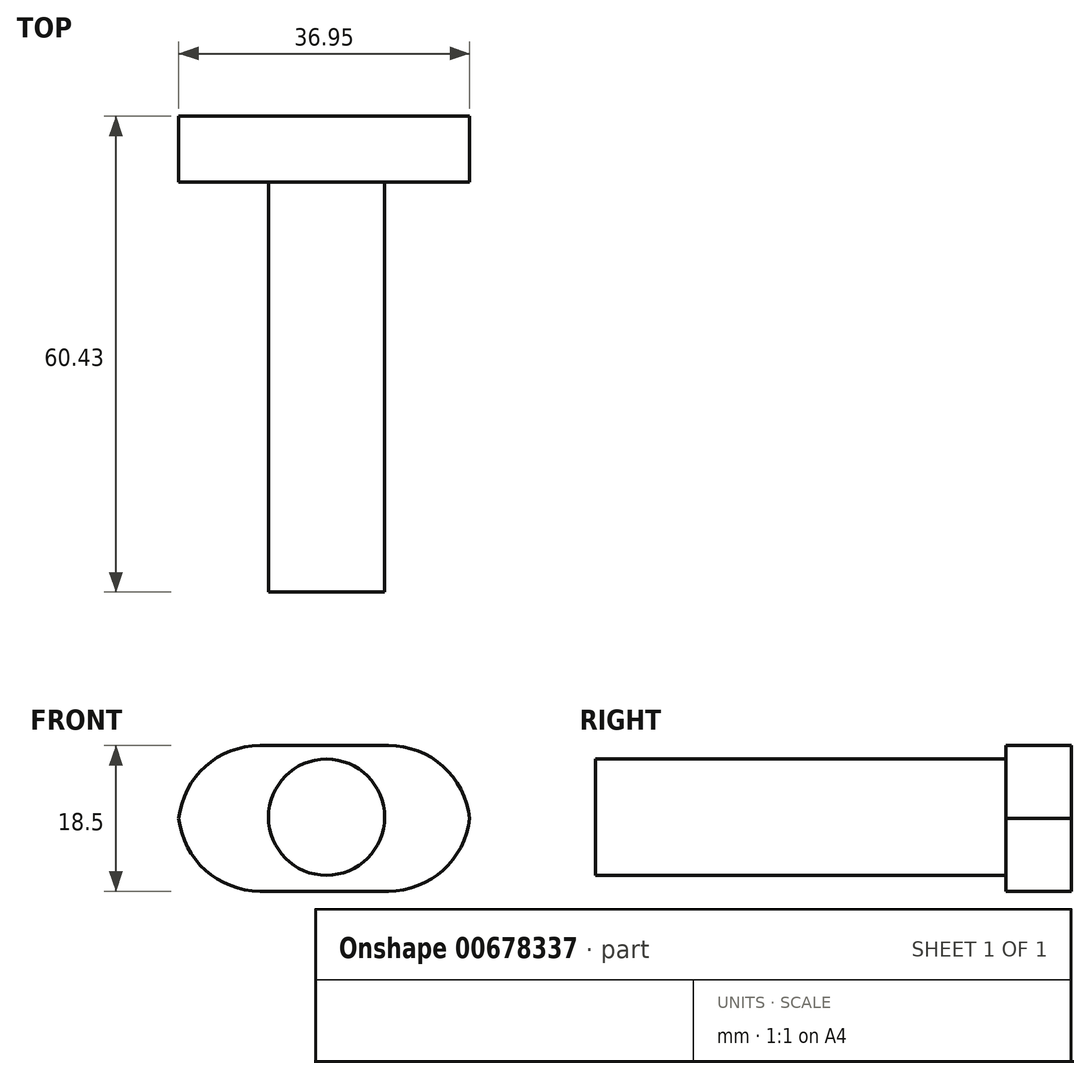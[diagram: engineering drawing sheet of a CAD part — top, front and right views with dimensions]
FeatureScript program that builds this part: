
annotation { "Feature Type Name" : "Feature", "Feature Type Description" : "" }
export const myFeature = defineFeature(function(context is Context, id is Id, definition is map)
    precondition{}
    {
        {
            var Q0;
            Q0=qCreatedBy(makeId("Front.planeOp"),FACE);
            var sketch = newSketch(context, id + "F0", { "sketchPlane" : qUnion([Q0])});
            skCircle(sketch, "E0", {"center": v(0, 0) * mm, "radius": 7.38 * mm});
            skSolve(sketch);
        }
        {
            var Q0;
            Q0=makeQuery(id+"F0.imprint","IMPRINT",FACE,{"disambiguationData":[TD([[makeQuery(id+"F0.imprint","IMPRINT",EDGE,{"derivedFrom":sQuery(id+"F0.wireOp",EDGE,"E0")}),1.0]])]});
            extrude(context, id + "F1", {"entities" : qUnion([Q0]), "depth" : 57.7 * mm, "offsetDistance" : 25 * mm});
        }
        {
            var Q0;
            Q0=qCreatedBy(makeId("Top.planeOp"),FACE);
            var sketch = newSketch(context, id + "F2", { "sketchPlane" : qUnion([Q0])});
            skLineSegment(sketch, "E1.bottom", {"start": v(-18.83, 2.73) * mm, "end": v(18.25, 2.73) * mm});
            skLineSegment(sketch, "E1.top", {"start": v(-18.83, -5.6) * mm, "end": v(18.25, -5.6) * mm});
            skLineSegment(sketch, "E1.left", {"start": v(-18.83, 2.73) * mm, "end": v(-18.83, -5.6) * mm});
            skLineSegment(sketch, "E1.right", {"start": v(18.25, 2.73) * mm, "end": v(18.25, -5.6) * mm});
            skSolve(sketch);
        }
        {
            var Q0;
            Q0=makeQuery(id+"F2.imprint","IMPRINT",FACE,{"disambiguationData":[TD([[makeQuery(id+"F2.imprint","IMPRINT",EDGE,{"derivedFrom":sQuery(id+"F2.wireOp",EDGE,"E1.bottom")}),-1.0]])]});
            extrude(context, id + "F3", {"entities" : qUnion([Q0]), "operationType" : NewBodyOperationType.ADD, "depth" : 9.1 * mm, "offsetDistance" : 25 * mm, "hasSecondDirection" : true, "secondDirectionOppositeDirection" : true, "secondDirectionDepth" : 9.4 * mm});
        }
        {
            var Q0;
            Q0=makeQuery(id+"F3.opExtrude","CAP_EDGE",EDGE,{"disambiguationData":[OSD([sQuery(id+"F2.wireOp",EDGE,"E1.left")])],"isStart":true});
            var Q1;
            Q1=makeQuery(id+"F3.opExtrude","CAP_EDGE",EDGE,{"disambiguationData":[OSD([sQuery(id+"F2.wireOp",EDGE,"E1.left")])],"isStart":false});
            var Q2;
            Q2=makeQuery(id+"F3.opExtrude","CAP_EDGE",EDGE,{"disambiguationData":[OSD([sQuery(id+"F2.wireOp",EDGE,"E1.right")])],"isStart":false});
            var Q3;
            Q3=makeQuery(id+"F3.opExtrude","CAP_EDGE",EDGE,{"disambiguationData":[OSD([sQuery(id+"F2.wireOp",EDGE,"E1.right")])],"isStart":true});
            fillet(context, id + "F4", {"entities" : qUnion([Q0, Q1, Q2, Q3]), "radius" : 10.38 * mm, "tangentPropagation" : true, "allowEdgeOverflow" : false});
        }
    });
